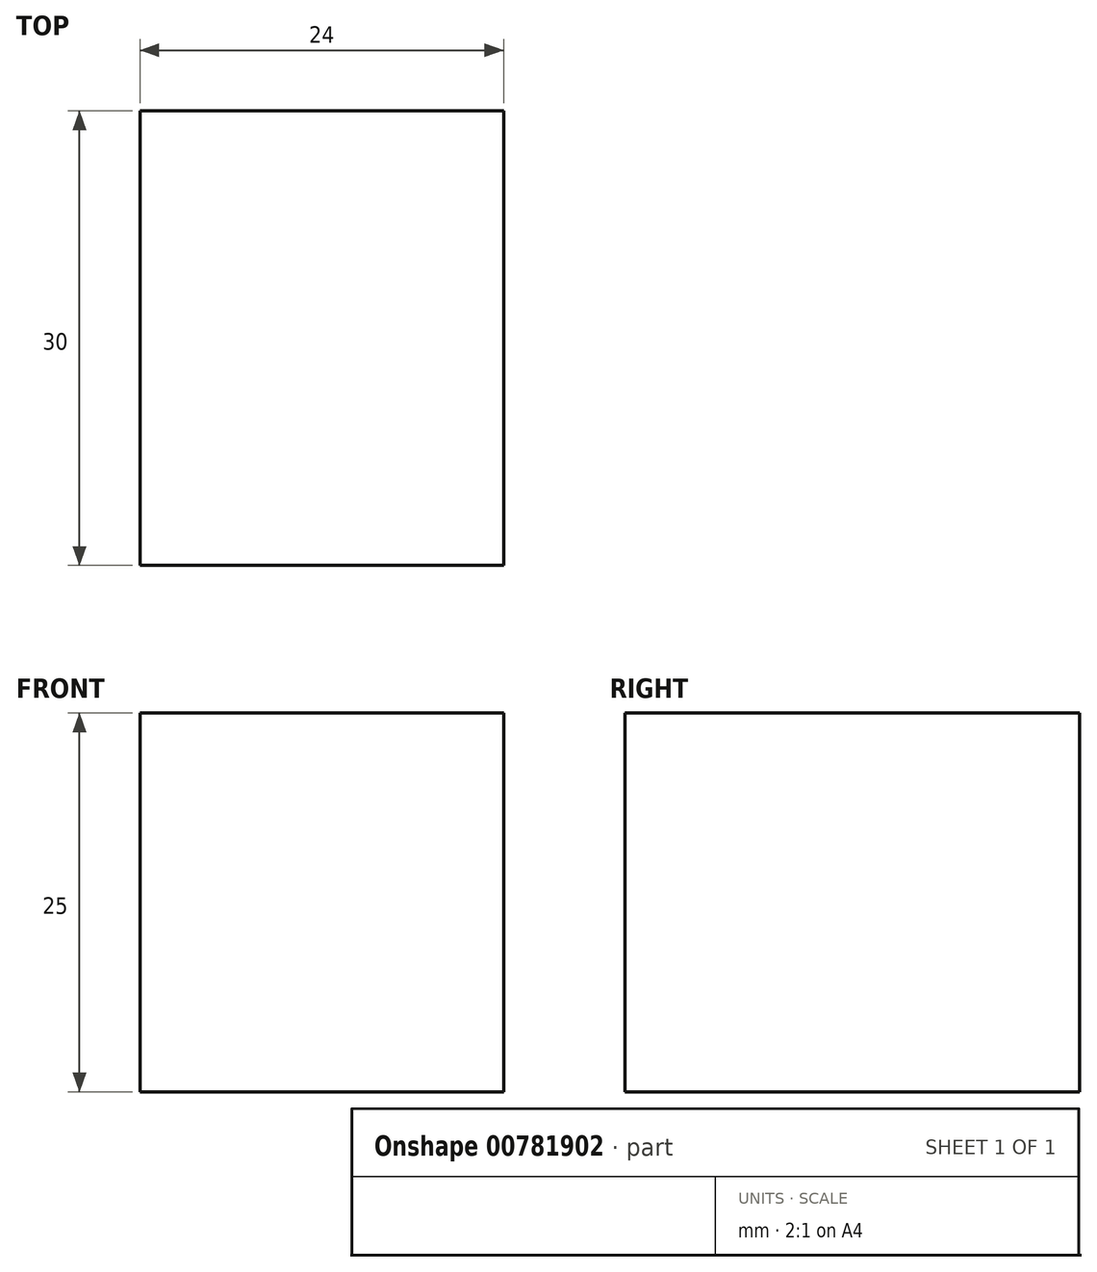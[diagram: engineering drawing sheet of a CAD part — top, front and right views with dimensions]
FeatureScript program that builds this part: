
annotation { "Feature Type Name" : "Feature", "Feature Type Description" : "" }
export const myFeature = defineFeature(function(context is Context, id is Id, definition is map)
    precondition{}
    {
        {
            var Q0;
            Q0=qCreatedBy(makeId("Front.planeOp"),FACE);
            var sketch = newSketch(context, id + "F0", { "sketchPlane" : qUnion([Q0])});
            skLineSegment(sketch, "E0.bottom", {"start": v(11.71, 12.54) * mm, "end": v(-13.29, 12.54) * mm});
            skLineSegment(sketch, "E0.top", {"start": v(11.71, -12.46) * mm, "end": v(-13.29, -12.46) * mm});
            skLineSegment(sketch, "E0.left", {"start": v(11.71, 12.54) * mm, "end": v(11.71, -12.46) * mm});
            skLineSegment(sketch, "E0.right", {"start": v(-12.29, 12.54) * mm, "end": v(-12.29, -12.46) * mm});
            skSolve(sketch);
        }
        {
            var Q0;
            Q0=qSketchRegion(id+"F0",true);
            extrude(context, id + "F1", {"entities" : qUnion([Q0]), "endBound" : BoundingType.SYMMETRIC, "depth" : 30 * mm, "offsetDistance" : 25 * mm});
        }
    });
